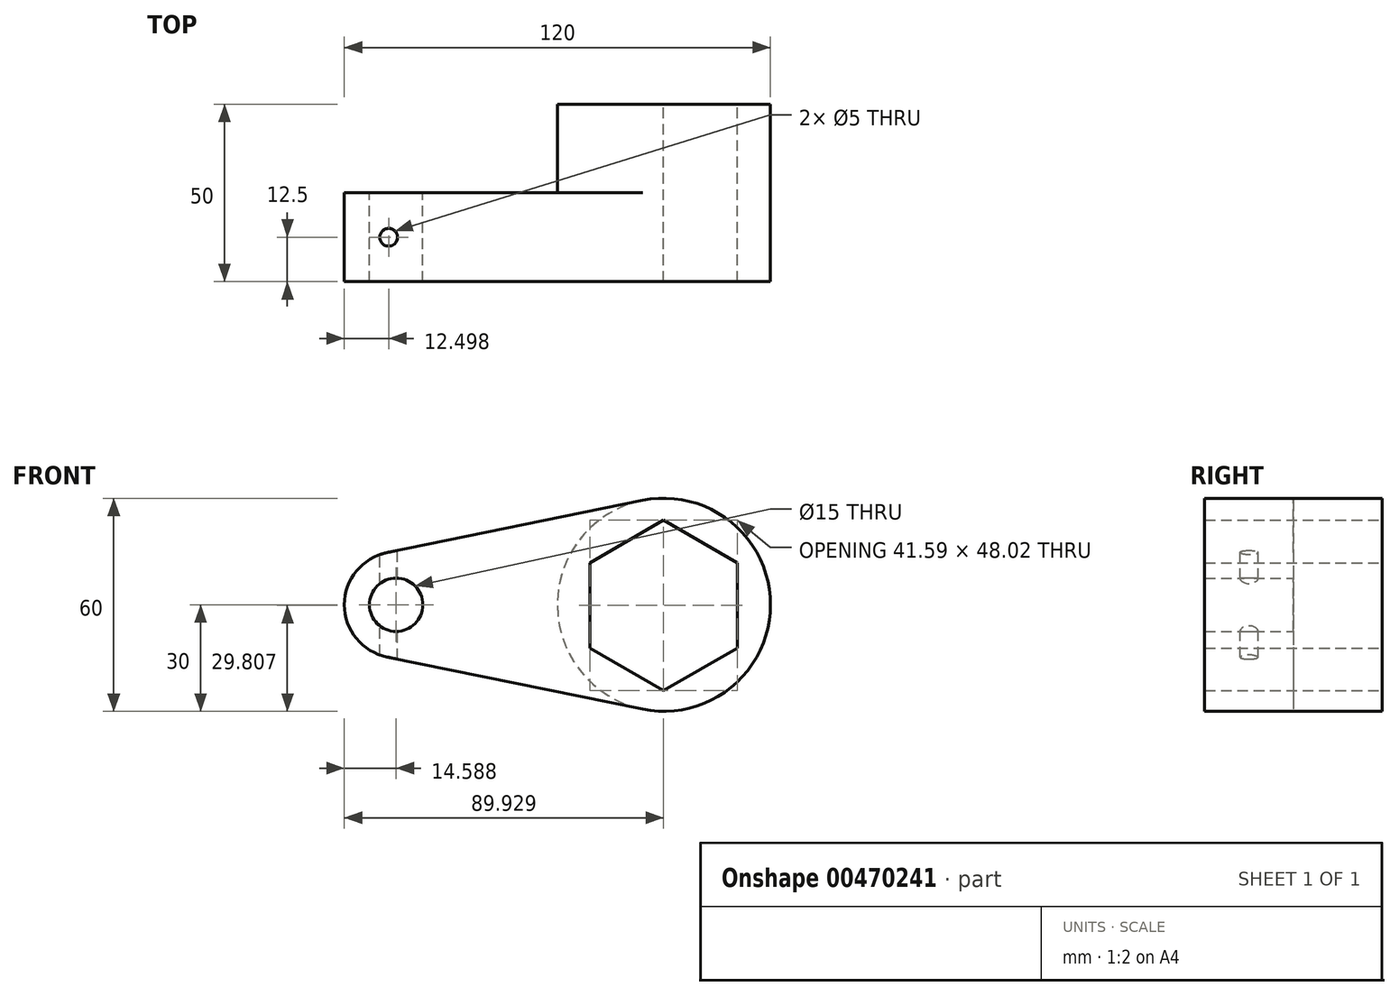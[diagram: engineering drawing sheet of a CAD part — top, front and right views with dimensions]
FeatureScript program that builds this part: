
annotation { "Feature Type Name" : "Feature", "Feature Type Description" : "" }
export const myFeature = defineFeature(function(context is Context, id is Id, definition is map)
    precondition{}
    {
        {
            var Q0;
            Q0=qCreatedBy(makeId("Front.planeOp"),FACE);
            var sketch = newSketch(context, id + "F0", { "sketchPlane" : qUnion([Q0])});
            skCircle(sketch, "E0", {"center": v(-35.65, 0) * mm, "radius": 15 * mm});
            skCircle(sketch, "E1", {"center": v(39.35, 0) * mm, "radius": 30 * mm});
            skLineSegment(sketch, "E2", {"start": v(-38.65, 14.7) * mm, "end": v(33.35, 29.4) * mm});
            skLineSegment(sketch, "E3", {"start": v(-38.65, -14.7) * mm, "end": v(33.35, -29.4) * mm});
            skSolve(sketch);
        }
        {
            var Q0;
            {var subQ0=sQuery(id+"F0.wireOp",EDGE,"E0");var subQ1=makeQuery(id+"F0.imprint","INTERSECT",VERTEX,{"derivedFrom":[subQ0,sQuery(id+"F0.wireOp",EDGE,"E2")]});Q0=makeQuery(id+"F0.imprint","IMPRINT",FACE,{"disambiguationData":[TD([[makeQuery(id+"F0.imprint","IMPRINT",EDGE,{"disambiguationData":[TD([[subQ1,-1.0]])],"derivedFrom":subQ0}),1.0]])]});}
            var Q1;
            {var subQ0=sQuery(id+"F0.wireOp",EDGE,"E2");Q1=makeQuery(id+"F0.imprint","IMPRINT",FACE,{"disambiguationData":[TD([[makeQuery(id+"F0.imprint","IMPRINT",EDGE,{"derivedFrom":subQ0}),-1.0]])]});}
            var Q2;
            {var subQ0=sQuery(id+"F0.wireOp",EDGE,"E1");var subQ1=makeQuery(id+"F0.imprint","INTERSECT",VERTEX,{"derivedFrom":[subQ0,sQuery(id+"F0.wireOp",EDGE,"E2")]});Q2=makeQuery(id+"F0.imprint","IMPRINT",FACE,{"disambiguationData":[TD([[makeQuery(id+"F0.imprint","IMPRINT",EDGE,{"disambiguationData":[TD([[subQ1,-1.0]])],"derivedFrom":subQ0}),1.0]])]});}
            extrude(context, id + "F1", {"entities" : qUnion([Q0, Q1, Q2]), "depth" : 25 * mm});
        }
        {
            var Q0;
            {var subQ0=sQuery(id+"F0.wireOp",EDGE,"E1");var subQ1=makeQuery(id+"F0.imprint","INTERSECT",VERTEX,{"derivedFrom":[subQ0,sQuery(id+"F0.wireOp",EDGE,"E2")]});Q0=makeQuery(id+"F0.imprint","IMPRINT",FACE,{"disambiguationData":[TD([[makeQuery(id+"F0.imprint","IMPRINT",EDGE,{"disambiguationData":[TD([[subQ1,-1.0]])],"derivedFrom":subQ0}),1.0]])]});}
            extrude(context, id + "F2", {"entities" : qUnion([Q0]), "operationType" : NewBodyOperationType.ADD, "depth" : 25 * mm});
        }
        {
            var Q0;
            {var subQ0=sQuery(id+"F0.wireOp",EDGE,"E1");var subQ1=makeQuery(id+"F0.imprint","INTERSECT",VERTEX,{"derivedFrom":[subQ0,sQuery(id+"F0.wireOp",EDGE,"E2")]});Q0=makeQuery(id+"F0.imprint","IMPRINT",FACE,{"disambiguationData":[TD([[makeQuery(id+"F0.imprint","IMPRINT",EDGE,{"disambiguationData":[TD([[subQ1,-1.0]])],"derivedFrom":subQ0}),1.0]])]});}
            var Q1;
            Q1=sQuery(id+"F0.wireOp",EDGE,"E1");
            extrude(context, id + "F3", {"entities" : qUnion([Q0]), "operationType" : NewBodyOperationType.ADD, "surfaceEntities" : qUnion([Q1]), "oppositeDirection" : true, "depth" : 25 * mm});
        }
        {
            var Q0;
            Q0=makeQuery(id+"F3.opExtrude","CAP_FACE",FACE,{"disambiguationData":[OSD([sQuery(id+"F0.wireOp",EDGE,"E1")])],"isStart":false});
            var sketch = newSketch(context, id + "F4", { "sketchPlane" : qUnion([Q0])});
            skCircle(sketch, "E4.cCircle", {"center": v(-39.28, -0.2) * mm, "radius": 20.8 * mm, "construction": true});
            skLineSegment(sketch, "E4.0", {"start": v(-18.48, 11.81) * mm, "end": v(-18.48, -12.2) * mm});
            skLineSegment(sketch, "E4.1", {"start": v(-18.48, -12.2) * mm, "end": v(-39.28, -24.2) * mm});
            skLineSegment(sketch, "E4.2", {"start": v(-39.28, -24.2) * mm, "end": v(-60.07, -12.2) * mm});
            skLineSegment(sketch, "E4.3", {"start": v(-60.07, -12.2) * mm, "end": v(-60.07, 11.81) * mm});
            skLineSegment(sketch, "E4.4", {"start": v(-60.07, 11.81) * mm, "end": v(-39.28, 23.82) * mm});
            skLineSegment(sketch, "E4.5", {"start": v(-39.28, 23.82) * mm, "end": v(-18.48, 11.81) * mm});
            skPoint(sketch, "E4.0.midPoint", {"position": v(-18.48, -0.2) * mm});
            skSolve(sketch);
        }
        {
            var Q0;
            Q0=makeQuery(id+"F1.opExtrude","CAP_FACE",FACE,{"disambiguationData":[OSD([sQuery(id+"F0.wireOp",EDGE,"E0"),sQuery(id+"F0.wireOp",EDGE,"E1"),sQuery(id+"F0.wireOp",EDGE,"E2"),sQuery(id+"F0.wireOp",EDGE,"E3")])],"isStart":false});
            extrude(context, id + "F5", {"entities" : qUnion([Q0]), "operationType" : NewBodyOperationType.REMOVE, "endBound" : BoundingType.THROUGH_ALL, "oppositeDirection" : true, "depth" : 25 * mm, "hasSecondDirection" : true, "secondDirectionOppositeDirection" : true, "secondDirectionDepth" : 25 * mm});
        }
        {
            var Q0;
            {var subQ0=sQuery(id+"F0.wireOp",EDGE,"E1");var subQ1=makeQuery(id+"F0.imprint","INTERSECT",VERTEX,{"derivedFrom":[subQ0,sQuery(id+"F0.wireOp",EDGE,"E2")]});Q0=makeQuery(id+"F0.imprint","IMPRINT",FACE,{"disambiguationData":[TD([[makeQuery(id+"F0.imprint","IMPRINT",EDGE,{"disambiguationData":[TD([[subQ1,-1.0]])],"derivedFrom":subQ0}),1.0]])]});}
            extrude(context, id + "F6", {"entities" : qUnion([Q0]), "operationType" : NewBodyOperationType.ADD, "oppositeDirection" : true, "depth" : 25 * mm});
        }
        {
            var Q0;
            Q0=makeQuery(id+"F4.imprint","IMPRINT",FACE,{"disambiguationData":[TD([[makeQuery(id+"F4.imprint","IMPRINT",EDGE,{"derivedFrom":sQuery(id+"F4.wireOp",EDGE,"E4.0")}),-1.0]])]});
            extrude(context, id + "F7", {"entities" : qUnion([Q0]), "operationType" : NewBodyOperationType.REMOVE, "endBound" : BoundingType.THROUGH_ALL, "oppositeDirection" : true, "depth" : 25 * mm});
        }
        {
            var Q0;
            {var subQ0=sQuery(id+"F0.wireOp",EDGE,"E0");var subQ1=makeQuery(id+"F0.imprint","INTERSECT",VERTEX,{"derivedFrom":[subQ0,sQuery(id+"F0.wireOp",EDGE,"E2")]});Q0=makeQuery(id+"F0.imprint","IMPRINT",FACE,{"disambiguationData":[TD([[makeQuery(id+"F0.imprint","IMPRINT",EDGE,{"disambiguationData":[TD([[subQ1,-1.0]])],"derivedFrom":subQ0}),1.0]])]});}
            var sketch = newSketch(context, id + "F8", { "sketchPlane" : qUnion([Q0])});
            skCircle(sketch, "E5", {"center": v(-36.06, 0) * mm, "radius": 7.5 * mm});
            skSolve(sketch);
        }
        {
            var Q0;
            Q0 = qSketchRegion(id + "F8", true);
            extrude(context, id + "F9", {"entities" : qUnion([Q0]), "operationType" : NewBodyOperationType.REMOVE, "depth" : 25 * mm});
        }
        {
            var Q0;
            Q0=qCreatedBy(makeId("Top.planeOp"),FACE);
            var sketch = newSketch(context, id + "F10", { "sketchPlane" : qUnion([Q0])});
            skCircle(sketch, "E6", {"center": v(-38.15, -12.5) * mm, "radius": 2.5 * mm});
            skSolve(sketch);
        }
        {
            var Q0;
            Q0 = qSketchRegion(id + "F10", true);
            extrude(context, id + "F11", {"entities" : qUnion([Q0]), "operationType" : NewBodyOperationType.REMOVE, "oppositeDirection" : true, "depth" : 25 * mm, "hasSecondDirection" : true, "secondDirectionOppositeDirection" : false, "secondDirectionDepth" : 25 * mm});
        }
    });
